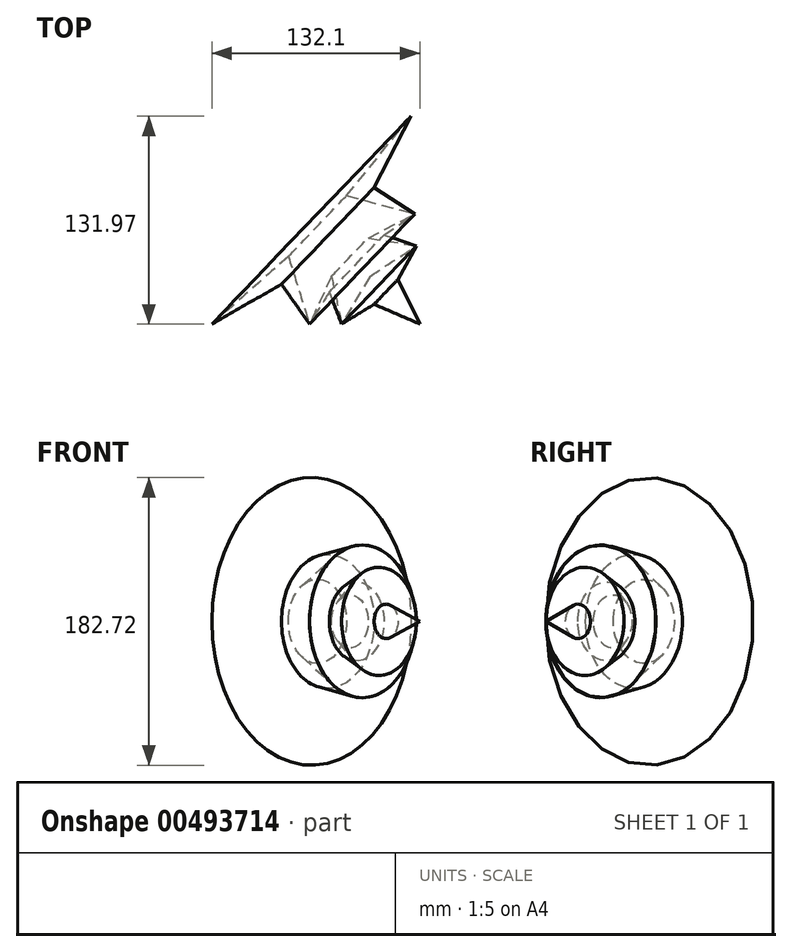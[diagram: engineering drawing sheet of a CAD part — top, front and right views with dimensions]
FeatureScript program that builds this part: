
annotation { "Feature Type Name" : "Feature", "Feature Type Description" : "" }
export const myFeature = defineFeature(function(context is Context, id is Id, definition is map)
    precondition{}
    {
        {
            var Q0;
            Q0=qCreatedBy(makeId("Top.planeOp"),FACE);
            var sketch = newSketch(context, id + "F0", { "sketchPlane" : qUnion([Q0])});
            skLineSegment(sketch, "E0", {"start": v(-58.53, 0) * mm, "end": v(-9.93, 42.96) * mm});
            skLineSegment(sketch, "E1", {"start": v(-9.93, 42.96) * mm, "end": v(3.5, 0) * mm});
            skLineSegment(sketch, "E2", {"start": v(3.5, 0) * mm, "end": v(17.45, 30.34) * mm});
            skLineSegment(sketch, "E3", {"start": v(17.45, 30.34) * mm, "end": v(23.9, 0) * mm});
            skLineSegment(sketch, "E4", {"start": v(23.9, 0) * mm, "end": v(41.88, 30.34) * mm});
            skLineSegment(sketch, "E5", {"start": v(41.88, 30.34) * mm, "end": v(73.57, 0) * mm});
            skLineSegment(sketch, "E6", {"start": v(73.57, 0) * mm, "end": v(44.57, 12.62) * mm});
            skLineSegment(sketch, "E7", {"start": v(44.57, 12.62) * mm, "end": v(23.9, 0) * mm});
            skLineSegment(sketch, "E8", {"start": v(23.9, 0) * mm, "end": v(16.08, 20.34) * mm});
            skLineSegment(sketch, "E9", {"start": v(16.08, 20.34) * mm, "end": v(3.5, 0) * mm});
            skLineSegment(sketch, "E10", {"start": v(3.5, 0) * mm, "end": v(-14.31, 25.3) * mm});
            skLineSegment(sketch, "E11", {"start": v(-14.31, 25.3) * mm, "end": v(-58.53, 0) * mm});
            skSolve(sketch);
        }
        {
            var Q0;
            Q0=makeQuery(id+"F0.imprint","IMPRINT",FACE,{"disambiguationData":[TD([[makeQuery(id+"F0.imprint","IMPRINT",EDGE,{"derivedFrom":sQuery(id+"F0.wireOp",EDGE,"E4")}),-1.0]])]});
            var Q1;
            Q1=makeQuery(id+"F0.imprint","IMPRINT",FACE,{"disambiguationData":[TD([[makeQuery(id+"F0.imprint","IMPRINT",EDGE,{"derivedFrom":sQuery(id+"F0.wireOp",EDGE,"E2")}),-1.0]])]});
            var Q2;
            Q2=makeQuery(id+"F0.imprint","IMPRINT",FACE,{"disambiguationData":[TD([[makeQuery(id+"F0.imprint","IMPRINT",EDGE,{"derivedFrom":sQuery(id+"F0.wireOp",EDGE,"E0")}),-1.0]])]});
            var Q3;
            Q3=sQuery(id+"F0.wireOp",EDGE,"E5");
            revolve(context, id + "F1", {"entities" : qUnion([Q0, Q1, Q2]), "axis" : qUnion([Q3]), "revolveType" : RevolveType.FULL});
        }
    });
